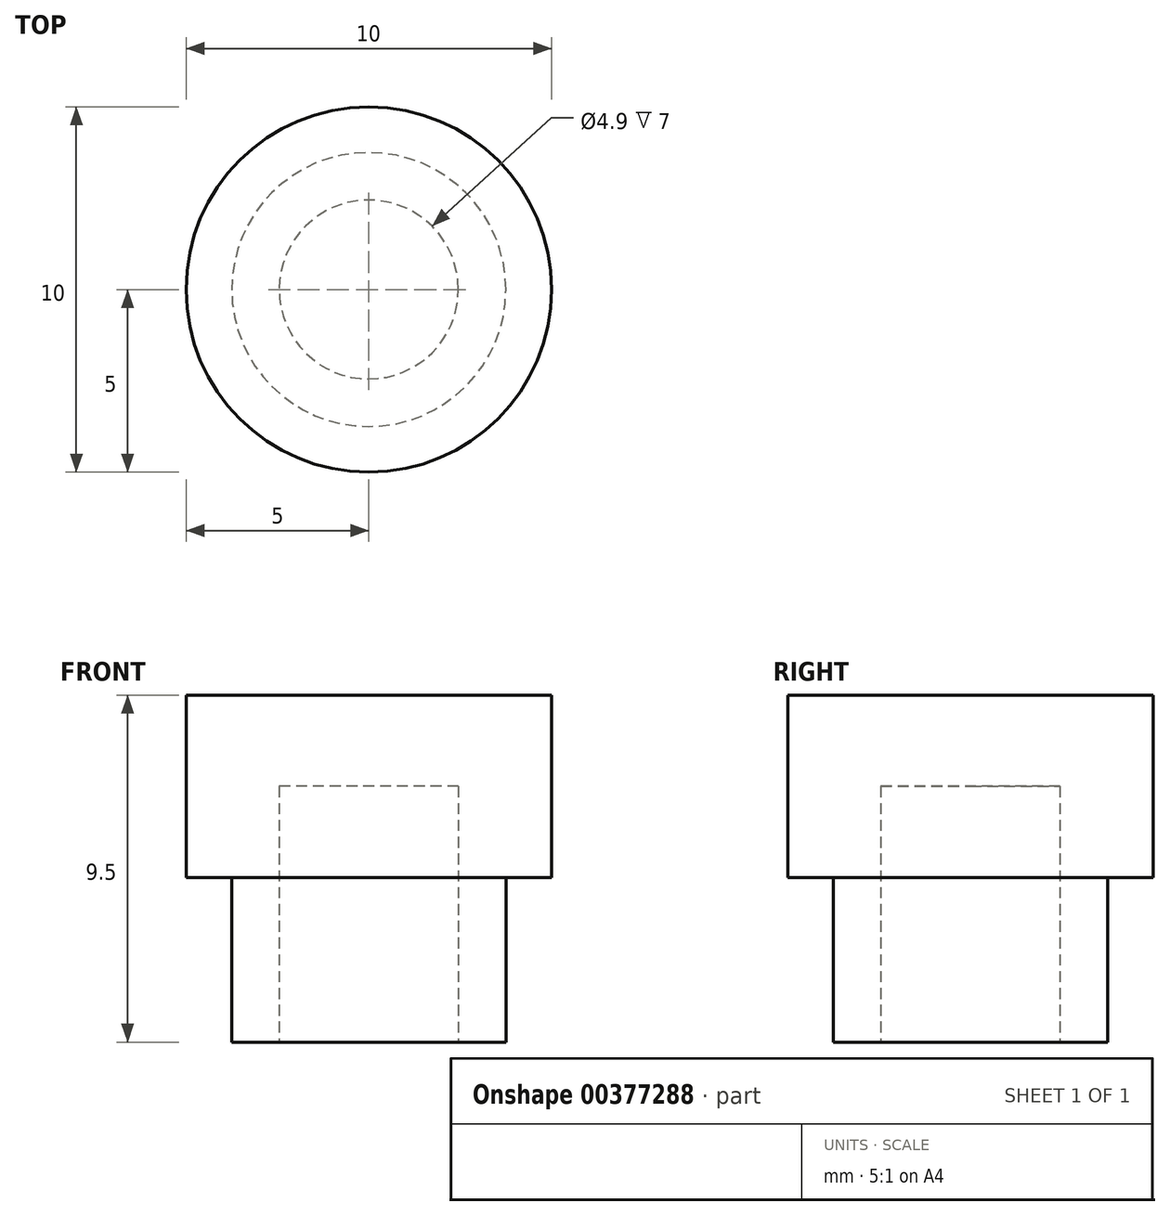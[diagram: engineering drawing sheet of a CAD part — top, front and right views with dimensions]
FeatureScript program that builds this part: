
annotation { "Feature Type Name" : "Feature", "Feature Type Description" : "" }
export const myFeature = defineFeature(function(context is Context, id is Id, definition is map)
    precondition{}
    {
        {
            var Q0;
            Q0=qCreatedBy(makeId("Top.planeOp"),FACE);
            var sketch = newSketch(context, id + "F0", { "sketchPlane" : qUnion([Q0])});
            skCircle(sketch, "E0", {"center": v(0, 0) * mm, "radius": 3.75 * mm});
            skCircle(sketch, "E1", {"center": v(0, 0) * mm, "radius": 2.45 * mm});
            skSolve(sketch);
        }
        {
            var Q0;
            Q0=qSketchRegion(id+"F0",true);
            extrude(context, id + "F1", {"entities" : qUnion([Q0]), "depth" : 4.5 * mm});
        }
        {
            var Q0;
            Q0=makeQuery(id+"F1.opExtrude","CAP_FACE",FACE,{"disambiguationData":[OSD([sQuery(id+"F0.wireOp",EDGE,"E0"),sQuery(id+"F0.wireOp",EDGE,"E1")])],"isStart":false});
            var sketch = newSketch(context, id + "F2", { "sketchPlane" : qUnion([Q0])});
            skCircle(sketch, "E2", {"center": v(0, 0) * mm, "radius": 5 * mm});
            skSolve(sketch);
        }
        {
            var Q0;
            Q0=qSketchRegion(id+"F2",true);
            extrude(context, id + "F3", {"entities" : qUnion([Q0]), "operationType" : NewBodyOperationType.ADD, "depth" : 5 * mm});
        }
        {
            var Q0;
            Q0=makeQuery(id+"F3.boolean.opBoolean","SPLIT",FACE,{"disambiguationData":[TD([makeQuery(id+"F1.opExtrude","SWEPT_FACE",FACE,{"disambiguationData":[OSD([sQuery(id+"F0.wireOp",EDGE,"E1")])]})])],"derivedFrom":makeQuery(id+"F3.opExtrude","CAP_FACE",FACE,{"disambiguationData":[OSD([sQuery(id+"F2.wireOp",EDGE,"E2")])],"isStart":true})});
            var sketch = newSketch(context, id + "F4", { "sketchPlane" : qUnion([Q0])});
            skCircle(sketch, "E3", {"center": v(0, 0) * mm, "radius": 2.45 * mm});
            skSolve(sketch);
        }
        {
            var Q0;
            Q0=qSketchRegion(id+"F4",true);
            extrude(context, id + "F5", {"entities" : qUnion([Q0]), "operationType" : NewBodyOperationType.REMOVE, "oppositeDirection" : true, "depth" : 2.5 * mm});
        }
    });
